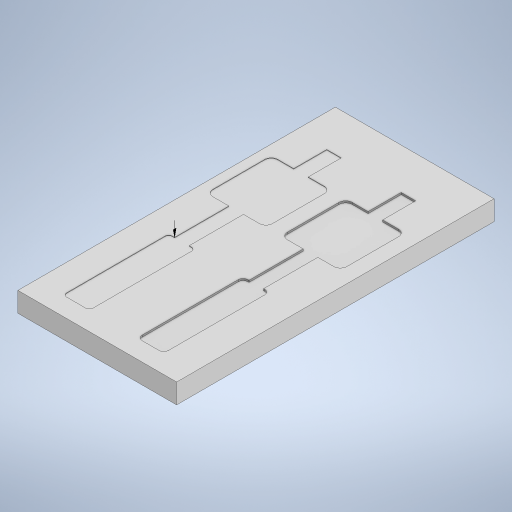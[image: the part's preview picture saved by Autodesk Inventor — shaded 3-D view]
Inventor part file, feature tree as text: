
AUTODESK INVENTOR PART (.ipt)
format: ipt  version: 2024.2 (Build 282272000, 272)  size: 310,784 bytes
history: native  units: in
note: dims shown in document units (in); Inventor stores cm internally (conversion verified against a paired STEP export)
features: extrude x3, sketch x3, other x2
ambient origin geometry x8: Origin, YZ Plane, XZ Plane, XY Plane, X Axis, Y Axis, Z Axis, Center Point
bodies: Solid1 (feature_tree)
feature tree (8):
  other  "Annotations"
  extrude  "Extrusion1"  Depth=6.0in
  extrude  "Extrusion2"  Depth=0.01in TaperAngle=0.0deg
  extrude  "Extrusion3"  Depth=0.5in
  sketch  "Sketch1"  dims[d0=3.0in d1=6.0in]
  sketch  "Sketch2"  dims[d2=0.375in d3=0.0in d8=0.01in d9=0.0in]
  sketch  "Sketch3"  dims[d11=2.0in d12=0.5in d13=0.0938in d14=0.035in d15=0.0in d17=0.0in d20=2.875in d22=0.0in d28=0.0in d33=0.0in d34=0.125in d36=1.025in d37=2.0in d40=1.025in d38=0.1308in d39=0.375in]
  other  "Linear Dimension 1"
